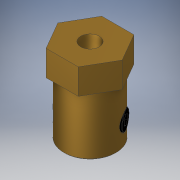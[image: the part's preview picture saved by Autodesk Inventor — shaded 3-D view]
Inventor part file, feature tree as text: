
AUTODESK INVENTOR PART (.ipt)
format: ipt  version: 2018 (Build 220112000, 112)  size: 268,288 bytes
history: native  units: in
note: dims shown in document units (in); Inventor stores cm internally (conversion verified against a paired STEP export)
features: extrude x6, sketch x6, chamfer x2, fillet x2, thread x2, plane x1
ambient origin geometry x8: Origin, YZ Plane, XZ Plane, XY Plane, X Axis, Y Axis, Z Axis, Center Point
bodies: Solid1 (feature_tree), Solid2 (feature_tree)
feature tree (19):
  extrude  "Extrusion1"  Depth=0.1969in
  extrude  "Extrusion2"  Depth=0.4724in
  extrude  "Extrusion3"  Depth=0.1575in
  plane  "Work Plane1"
  extrude  "Extrusion4"  Depth=0.1575in
  chamfer  "Chamfer1"  Distance=0.654in
  fillet  "Fillet1"  Radius=0.0039in
  fillet  "Fillet2"  Radius=0.0039in
  thread  "Thread1"  [1 undecoded]
  thread  "Thread2"  [1 undecoded]
  extrude  "Extrusion5"  Depth=0.1457in TaperAngle=0.0deg
  chamfer  "Chamfer2"  Distance=0.0039in Angle=45.0deg
  extrude  "Extrusion6"  Depth=0.0394in TaperAngle=0.0deg
  sketch  "Sketch1"  dims[d0=0.4449in d1=0.1969in]
  sketch  "Sketch2"  dims[d2=0.7126in d3=0.0in d4=0.4724in]
  sketch  "Sketch3"  dims[d5=0.2165in d6=0.0in d7=0.1575in]
  sketch  "Sketch4"  dims[d8=0.2165in d9=0.0in d10=0.1575in]
  sketch  "Sketch5"  dims[d11=0.1772in d12=0.654in d13=0.0in]
  sketch  "Sketch6"  dims[d14=0.0079in d15=0.0787in d16=45.0deg d17=0.0039in d18=0.0039in d19=0.3937in d20=0.0in d21=0.3937in d22=0.0in d23=0.1457in d24=0.0in d25=0.0039in d26=0.0787in d27=45.0deg d28=0.0394in d29=0.0in]
note: 2 required parameter values undecoded (feature->parameter linkage not recoverable at this tier; creation-order binding heuristic only, values carry confidence <= 0.55)
